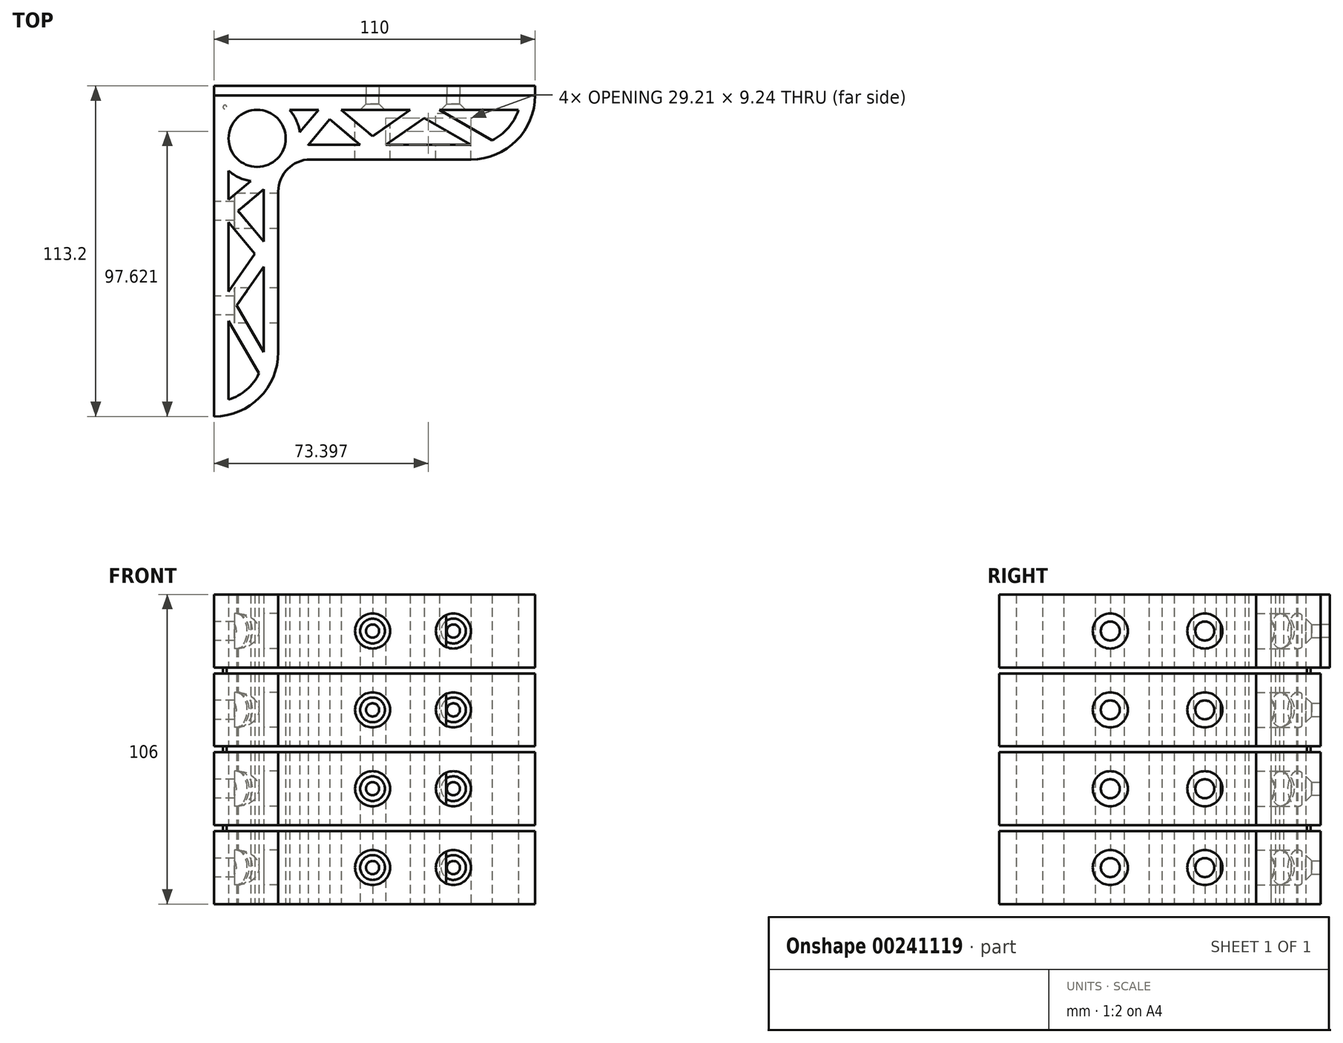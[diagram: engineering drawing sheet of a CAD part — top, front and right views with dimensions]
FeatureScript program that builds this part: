
annotation { "Feature Type Name" : "Feature", "Feature Type Description" : "" }
export const myFeature = defineFeature(function(context is Context, id is Id, definition is map)
    precondition{}
    {
        {
            var Q0;
            Q0=qCreatedBy(makeId("Top.planeOp"),FACE);
            var sketch = newSketch(context, id + "F0", { "sketchPlane" : qUnion([Q0])});
            skLineSegment(sketch, "E0", {"start": v(0, 0) * mm, "end": v(0, 110) * mm});
            skLineSegment(sketch, "E1", {"start": v(0, 110) * mm, "end": v(110, 0) * mm, "construction": true});
            skLineSegment(sketch, "E2", {"start": v(110, 0) * mm, "end": v(0, 0) * mm, "construction": true});
            skArc(sketch, "E3", {"start": v(0, 0) * mm, "mid": v(15.56, 6.44) * mm, "end": v(22, 22) * mm});
            skLineSegment(sketch, "E4", {"start": v(22, 22) * mm, "end": v(22, 77) * mm});
            skArc(sketch, "E5", {"start": v(25.22, 84.78) * mm, "mid": v(22.84, 81.2) * mm, "end": v(22, 77) * mm});
            skLineSegment(sketch, "E6", {"start": v(0, 110) * mm, "end": v(25.22, 84.78) * mm});
            skLineSegment(sketch, "E7.0", {"start": v(5, 5.75) * mm, "end": v(5, 105) * mm});
            skArc(sketch, "E7.1", {"start": v(5, 5.75) * mm, "mid": v(13.67, 11.9) * mm, "end": v(17, 22) * mm});
            skLineSegment(sketch, "E7.2", {"start": v(17, 22) * mm, "end": v(17, 77) * mm});
            skArc(sketch, "E7.3", {"start": v(21.69, 88.31) * mm, "mid": v(18.22, 83.12) * mm, "end": v(17, 77) * mm});
            skLineSegment(sketch, "E8", {"start": v(15.4, 14.78) * mm, "end": v(5, 32.78) * mm});
            skLineSegment(sketch, "E9", {"start": v(5, 42.78) * mm, "end": v(17, 22) * mm});
            skLineSegment(sketch, "E10", {"start": v(5, 42.78) * mm, "end": v(17, 59.92) * mm});
            skLineSegment(sketch, "E11", {"start": v(17, 59.92) * mm, "end": v(5, 74.22) * mm});
            skLineSegment(sketch, "E12", {"start": v(5, 66.44) * mm, "end": v(14.03, 55.68) * mm});
            skLineSegment(sketch, "E13", {"start": v(7.76, 38) * mm, "end": v(17, 51.2) * mm});
            skLineSegment(sketch, "E14", {"start": v(5, 32.78) * mm, "end": v(9.33, 35.28) * mm, "construction": true});
            skLineSegment(sketch, "E15", {"start": v(5, 42.78) * mm, "end": v(9.1, 39.92) * mm, "construction": true});
            skLineSegment(sketch, "E16", {"start": v(17, 59.92) * mm, "end": v(13.17, 56.7) * mm, "construction": true});
            skLineSegment(sketch, "E17", {"start": v(5, 74.22) * mm, "end": v(21.25, 87.85) * mm});
            skLineSegment(sketch, "E18", {"start": v(8.21, 70.4) * mm, "end": v(17, 77.77) * mm});
            skLineSegment(sketch, "E19", {"start": v(17, 77.77) * mm, "end": v(13.79, 81.6) * mm, "construction": true});
            skLineSegment(sketch, "E20", {"start": v(17, 77.77) * mm, "end": v(17.02, 77.78) * mm});
            skCircle(sketch, "E21", {"center": v(14.77, 95.23) * mm, "radius": 9.77 * mm});
            skArc(sketch, "E22", {"start": v(5, 84.15) * mm, "mid": v(8.55, 81.83) * mm, "end": v(12.61, 80.61) * mm});
            skLineSegment(sketch, "E23", {"start": v(14.77, 95.23) * mm, "end": v(5, 84.15) * mm, "construction": true});
            skPoint(sketch, "E24", {"position": v(8.3, 87.9) * mm});
            skSolve(sketch);
        }
        {
            var Q0;
            {var subQ0=sQuery(id+"F0.wireOp",EDGE,"E7.0");var subQ1=sQuery(id+"F0.wireOp",EDGE,"E6");var subQ2=makeQuery(id+"F0.imprint","INTERSECT",VERTEX,{"derivedFrom":[subQ1,subQ0]});Q0=makeQuery(id+"F0.imprint","IMPRINT",FACE,{"disambiguationData":[TD([[makeQuery(id+"F0.imprint","IMPRINT",EDGE,{"disambiguationData":[TD([[subQ2,-1.0]])],"derivedFrom":subQ1}),-1.0]])]});}
            var Q1;
            {var subQ14=sQuery(id+"F0.wireOp",EDGE,"E0");Q1=makeQuery(id+"F0.imprint","IMPRINT",FACE,{"disambiguationData":[TD([[makeQuery(id+"F0.imprint","IMPRINT",EDGE,{"derivedFrom":subQ14}),-1.0]])]});}
            var Q2;
            {var subQ3=sQuery(id+"F0.wireOp",EDGE,"E22");Q2=makeQuery(id+"F0.imprint","IMPRINT",FACE,{"disambiguationData":[TD([[makeQuery(id+"F0.imprint","IMPRINT",EDGE,{"derivedFrom":subQ3}),1.0]])]});}
            var Q3;
            {var subQ6=sQuery(id+"F0.wireOp",EDGE,"E18");Q3=makeQuery(id+"F0.imprint","IMPRINT",FACE,{"disambiguationData":[TD([[makeQuery(id+"F0.imprint","IMPRINT",EDGE,{"derivedFrom":subQ6}),1.0]])]});}
            var Q4;
            {var subQ6=sQuery(id+"F0.wireOp",EDGE,"E12");Q4=makeQuery(id+"F0.imprint","IMPRINT",FACE,{"disambiguationData":[TD([[makeQuery(id+"F0.imprint","IMPRINT",EDGE,{"derivedFrom":subQ6}),1.0]])]});}
            var Q5;
            {var subQ6=sQuery(id+"F0.wireOp",EDGE,"E13");Q5=makeQuery(id+"F0.imprint","IMPRINT",FACE,{"disambiguationData":[TD([[makeQuery(id+"F0.imprint","IMPRINT",EDGE,{"derivedFrom":subQ6}),1.0]])]});}
            var Q6;
            {var subQ0=sQuery(id+"F0.wireOp",EDGE,"E8");Q6=makeQuery(id+"F0.imprint","IMPRINT",FACE,{"disambiguationData":[TD([[makeQuery(id+"F0.imprint","IMPRINT",EDGE,{"derivedFrom":subQ0}),-1.0]])]});}
            extrude(context, id + "F1", {"entities" : qUnion([Q0, Q1, Q2, Q3, Q4, Q5, Q6]), "depth" : 25 * mm});
        }
        {
            var Q0;
            Q0=makeQuery(id+"F1.opExtrude","SWEPT_BODY",BODY,{"disambiguationData":[OSD([sQuery(id+"F0.wireOp",EDGE,"E0"),sQuery(id+"F0.wireOp",EDGE,"E3"),sQuery(id+"F0.wireOp",EDGE,"E4"),sQuery(id+"F0.wireOp",EDGE,"E5"),sQuery(id+"F0.wireOp",EDGE,"E6"),sQuery(id+"F0.wireOp",EDGE,"E7.0"),sQuery(id+"F0.wireOp",EDGE,"E7.1"),sQuery(id+"F0.wireOp",EDGE,"E7.2"),sQuery(id+"F0.wireOp",EDGE,"E7.3"),sQuery(id+"F0.wireOp",EDGE,"E8"),sQuery(id+"F0.wireOp",EDGE,"E9"),sQuery(id+"F0.wireOp",EDGE,"E10"),sQuery(id+"F0.wireOp",EDGE,"E11"),sQuery(id+"F0.wireOp",EDGE,"E12"),sQuery(id+"F0.wireOp",EDGE,"E13"),sQuery(id+"F0.wireOp",EDGE,"E17"),sQuery(id+"F0.wireOp",EDGE,"E18"),sQuery(id+"F0.wireOp",EDGE,"1766ab4e-5819-43f3-8559-5bc0afbba3c0.1"),sQuery(id+"F0.wireOp",EDGE,"1766ab4e-5819-43f3-8559-5bc0afbba3c0.2"),sQuery(id+"F0.wireOp",EDGE,"9d0f0dcf-438d-4fe8-bd9b-4e4da783941b.1"),sQuery(id+"F0.wireOp",EDGE,"9d0f0dcf-438d-4fe8-bd9b-4e4da783941b.3"),sQuery(id+"F0.wireOp",EDGE,"9d0f0dcf-438d-4fe8-bd9b-4e4da783941b.4"),sQuery(id+"F0.wireOp",EDGE,"E20")])]});
            var Q1;
            {var subQ0=sQuery(id+"F0.wireOp",EDGE,"E6");var subQ1=makeQuery(id+"F0.imprint","INTERSECT",VERTEX,{"derivedFrom":[subQ0,sQuery(id+"F0.wireOp",EDGE,"1766ab4e-5819-43f3-8559-5bc0afbba3c0.3")]});var subQ2=makeQuery(id+"F0.imprint","INTERSECT",VERTEX,{"derivedFrom":[subQ0,sQuery(id+"F0.wireOp",EDGE,"E7.0")]});Q1=makeQuery(id+"F1.opExtrude","SWEPT_FACE",FACE,{"disambiguationData":[OSD([subQ0]),TDD([makeQuery(id+"F0.imprint","IMPRINT",EDGE,{"disambiguationData":[TD([[makeQuery(id+"F0.imprint","INTERSECT",VERTEX,{"derivedFrom":[sQuery(id+"F0.wireOp",EDGE,"E0"),subQ0]}),-1.0]])],"derivedFrom":subQ0}),makeQuery(id+"F0.imprint","IMPRINT",EDGE,{"disambiguationData":[TD([[subQ2,-1.0]])],"derivedFrom":subQ0}),makeQuery(id+"F0.imprint","IMPRINT",EDGE,{"disambiguationData":[TD([[subQ1,-1.0]])],"derivedFrom":subQ0})])]});}
            mirror(context, id + "F2", {"operationType" : NewBodyOperationType.ADD, "entities" : qUnion([Q0]), "mirrorPlane" : qUnion([Q1])});
        }
        {
            var Q0;
            Q0=makeQuery(id+"F1.opExtrude","SWEPT_FACE",FACE,{"disambiguationData":[OSD([sQuery(id+"F0.wireOp",EDGE,"E0")])]});
            var sketch = newSketch(context, id + "F3", { "sketchPlane" : qUnion([Q0])});
            skLineSegment(sketch, "E25", {"start": v(-110, 12.5) * mm, "end": v(0, 12.5) * mm, "construction": true});
            skCircle(sketch, "E26", {"center": v(-70.4, 12.5) * mm, "radius": 3.25 * mm});
            skCircle(sketch, "E27", {"center": v(-38, 12.5) * mm, "radius": 3.25 * mm});
            skCircle(sketch, "E28", {"center": v(-70.4, 12.5) * mm, "radius": 6 * mm});
            skCircle(sketch, "E29", {"center": v(-38, 12.5) * mm, "radius": 6 * mm});
            skSolve(sketch);
        }
        {
            var Q0;
            Q0=makeQuery(id+"F2.opPattern","COPY",FACE,{"derivedFrom":makeQuery(id+"F1.opExtrude","SWEPT_FACE",FACE,{"disambiguationData":[OSD([sQuery(id+"F0.wireOp",EDGE,"E0")])]}),"instanceName":"1"});
            var sketch = newSketch(context, id + "F4", { "sketchPlane" : qUnion([Q0])});
            skLineSegment(sketch, "E30", {"start": v(0, 12.5) * mm, "end": v(-110, 12.5) * mm, "construction": true});
            skCircle(sketch, "E31", {"center": v(-54.32, 12.5) * mm, "radius": 2.25 * mm});
            skCircle(sketch, "E32", {"center": v(-82, 12.5) * mm, "radius": 2.25 * mm});
            skCircle(sketch, "E33", {"center": v(-82, 12.5) * mm, "radius": 6 * mm});
            skCircle(sketch, "E34", {"center": v(-54.32, 12.5) * mm, "radius": 6 * mm});
            skPoint(sketch, "E35", {"position": v(-88, 12.5) * mm});
            skSolve(sketch);
        }
        {
            var Q0;
            Q0=makeQuery(id+"F3.imprint","IMPRINT",FACE,{"disambiguationData":[TD([[makeQuery(id+"F3.imprint","IMPRINT",EDGE,{"derivedFrom":sQuery(id+"F3.wireOp",EDGE,"E26")}),1.0]])]});
            var Q1;
            Q1=makeQuery(id+"F3.imprint","IMPRINT",FACE,{"disambiguationData":[TD([[makeQuery(id+"F3.imprint","IMPRINT",EDGE,{"derivedFrom":sQuery(id+"F3.wireOp",EDGE,"E27")}),1.0]])]});
            extrude(context, id + "F5", {"entities" : qUnion([Q0, Q1]), "operationType" : NewBodyOperationType.REMOVE, "oppositeDirection" : true, "depth" : 25 * mm});
        }
        {
            var Q0;
            Q0=makeQuery(id+"F3.imprint","IMPRINT",FACE,{"disambiguationData":[TD([[makeQuery(id+"F3.imprint","IMPRINT",EDGE,{"derivedFrom":sQuery(id+"F3.wireOp",EDGE,"E26")}),-1.0]])]});
            var Q1;
            Q1=makeQuery(id+"F3.imprint","IMPRINT",FACE,{"disambiguationData":[TD([[makeQuery(id+"F3.imprint","IMPRINT",EDGE,{"derivedFrom":sQuery(id+"F3.wireOp",EDGE,"E27")}),-1.0]])]});
            extrude(context, id + "F6", {"entities" : qUnion([Q0, Q1]), "operationType" : NewBodyOperationType.REMOVE, "oppositeDirection" : true, "depth" : 25 * mm, "hasSecondDirection" : true, "secondDirectionOppositeDirection" : true, "secondDirectionDepth" : 7 * mm});
        }
        {
            var Q0;
            Q0=makeQuery(id+"F4.imprint","IMPRINT",FACE,{"disambiguationData":[TD([[makeQuery(id+"F4.imprint","IMPRINT",EDGE,{"derivedFrom":sQuery(id+"F4.wireOp",EDGE,"E32")}),1.0]])]});
            var Q1;
            Q1=makeQuery(id+"F4.imprint","IMPRINT",FACE,{"disambiguationData":[TD([[makeQuery(id+"F4.imprint","IMPRINT",EDGE,{"derivedFrom":sQuery(id+"F4.wireOp",EDGE,"E31")}),1.0]])]});
            extrude(context, id + "F7", {"entities" : qUnion([Q0, Q1]), "operationType" : NewBodyOperationType.REMOVE, "oppositeDirection" : true, "depth" : 25 * mm});
        }
        {
            var Q0;
            Q0=makeQuery(id+"F4.imprint","IMPRINT",FACE,{"disambiguationData":[TD([[makeQuery(id+"F4.imprint","IMPRINT",EDGE,{"derivedFrom":sQuery(id+"F4.wireOp",EDGE,"E31")}),-1.0]])]});
            var Q1;
            Q1=makeQuery(id+"F4.imprint","IMPRINT",FACE,{"disambiguationData":[TD([[makeQuery(id+"F4.imprint","IMPRINT",EDGE,{"derivedFrom":sQuery(id+"F4.wireOp",EDGE,"E32")}),-1.0]])]});
            extrude(context, id + "F8", {"entities" : qUnion([Q0, Q1]), "operationType" : NewBodyOperationType.REMOVE, "oppositeDirection" : true, "depth" : 25 * mm, "hasSecondDirection" : true, "secondDirectionOppositeDirection" : true, "secondDirectionDepth" : 6.3 * mm});
        }
        {
            var Q0;
            {var subQ0=sQuery(id+"F0.wireOp",EDGE,"E7.0");Q0=makeQuery(id+"F7.boolean.opBoolean","INTERSECT",EDGE,{"derivedFrom":[makeQuery(id+"F2.opPattern","COPY",FACE,{"derivedFrom":makeQuery(id+"F1.opExtrude","SWEPT_FACE",FACE,{"disambiguationData":[OSD([subQ0]),TDD([makeQuery(id+"F0.imprint","IMPRINT",EDGE,{"disambiguationData":[TD([[makeQuery(id+"F0.imprint","INTERSECT",VERTEX,{"derivedFrom":[subQ0,sQuery(id+"F0.wireOp",EDGE,"E12")]}),1.0]])],"derivedFrom":subQ0})])]}),"instanceName":"1"}),makeQuery(id+"F7.opExtrude","SWEPT_FACE",FACE,{"disambiguationData":[OSD([sQuery(id+"F4.wireOp",EDGE,"E31")])]})]});}
            var Q1;
            {var subQ0=sQuery(id+"F0.wireOp",EDGE,"E7.0");Q1=makeQuery(id+"F7.boolean.opBoolean","INTERSECT",EDGE,{"derivedFrom":[makeQuery(id+"F2.opPattern","COPY",FACE,{"derivedFrom":makeQuery(id+"F1.opExtrude","SWEPT_FACE",FACE,{"disambiguationData":[OSD([subQ0]),TDD([makeQuery(id+"F0.imprint","IMPRINT",EDGE,{"disambiguationData":[TD([[makeQuery(id+"F0.imprint","INTERSECT",VERTEX,{"derivedFrom":[subQ0,sQuery(id+"F0.wireOp",EDGE,"E7.1")]}),-1.0]])],"derivedFrom":subQ0})])]}),"instanceName":"1"}),makeQuery(id+"F7.opExtrude","SWEPT_FACE",FACE,{"disambiguationData":[OSD([sQuery(id+"F4.wireOp",EDGE,"E32")])]})]});}
            chamfer(context, id + "F9", {"entities" : qUnion([Q0, Q1]), "width" : 2 * mm, "tangentPropagation" : true});
        }
        {
            var Q0;
            Q0=makeQuery(id+"F1.opExtrude","SWEPT_BODY",BODY,{"disambiguationData":[OSD([sQuery(id+"F0.wireOp",EDGE,"E0"),sQuery(id+"F0.wireOp",EDGE,"E3"),sQuery(id+"F0.wireOp",EDGE,"E4"),sQuery(id+"F0.wireOp",EDGE,"E5"),sQuery(id+"F0.wireOp",EDGE,"E6"),sQuery(id+"F0.wireOp",EDGE,"E7.0"),sQuery(id+"F0.wireOp",EDGE,"E7.1"),sQuery(id+"F0.wireOp",EDGE,"E7.2"),sQuery(id+"F0.wireOp",EDGE,"E7.3"),sQuery(id+"F0.wireOp",EDGE,"E8"),sQuery(id+"F0.wireOp",EDGE,"E9"),sQuery(id+"F0.wireOp",EDGE,"E10"),sQuery(id+"F0.wireOp",EDGE,"E11"),sQuery(id+"F0.wireOp",EDGE,"E12"),sQuery(id+"F0.wireOp",EDGE,"E13"),sQuery(id+"F0.wireOp",EDGE,"E17"),sQuery(id+"F0.wireOp",EDGE,"E18"),sQuery(id+"F0.wireOp",EDGE,"E20"),sQuery(id+"F0.wireOp",EDGE,"E21"),sQuery(id+"F0.wireOp",EDGE,"E22")])]});
            transform(context, id + "F10", {"entities" : qUnion([Q0]), "transformType" : TransformType.TRANSLATION_3D, "dx" : 0 * mm, "dy" : 0 * mm, "dz" : 27 * mm, "makeCopy" : true});
        }
        {
            var Q0;
            Q0=makeQuery(id+"F10.opPattern","COPY",BODY,{"derivedFrom":makeQuery(id+"F1.opExtrude","SWEPT_BODY",BODY,{"disambiguationData":[OSD([sQuery(id+"F0.wireOp",EDGE,"E0"),sQuery(id+"F0.wireOp",EDGE,"E3"),sQuery(id+"F0.wireOp",EDGE,"E4"),sQuery(id+"F0.wireOp",EDGE,"E5"),sQuery(id+"F0.wireOp",EDGE,"E6"),sQuery(id+"F0.wireOp",EDGE,"E7.0"),sQuery(id+"F0.wireOp",EDGE,"E7.1"),sQuery(id+"F0.wireOp",EDGE,"E7.2"),sQuery(id+"F0.wireOp",EDGE,"E7.3"),sQuery(id+"F0.wireOp",EDGE,"E8"),sQuery(id+"F0.wireOp",EDGE,"E9"),sQuery(id+"F0.wireOp",EDGE,"E10"),sQuery(id+"F0.wireOp",EDGE,"E11"),sQuery(id+"F0.wireOp",EDGE,"E12"),sQuery(id+"F0.wireOp",EDGE,"E13"),sQuery(id+"F0.wireOp",EDGE,"E17"),sQuery(id+"F0.wireOp",EDGE,"E18"),sQuery(id+"F0.wireOp",EDGE,"E20"),sQuery(id+"F0.wireOp",EDGE,"E21"),sQuery(id+"F0.wireOp",EDGE,"E22")])]}),"instanceName":"1"});
            transform(context, id + "F11", {"entities" : qUnion([Q0]), "transformType" : TransformType.TRANSLATION_3D, "dx" : 0 * mm, "dy" : 0 * mm, "dz" : 27 * mm, "makeCopy" : true});
        }
        {
            var Q0;
            Q0=makeQuery(id+"F11.opPattern","COPY",BODY,{"derivedFrom":makeQuery(id+"F10.opPattern","COPY",BODY,{"derivedFrom":makeQuery(id+"F1.opExtrude","SWEPT_BODY",BODY,{"disambiguationData":[OSD([sQuery(id+"F0.wireOp",EDGE,"E0"),sQuery(id+"F0.wireOp",EDGE,"E3"),sQuery(id+"F0.wireOp",EDGE,"E4"),sQuery(id+"F0.wireOp",EDGE,"E5"),sQuery(id+"F0.wireOp",EDGE,"E6"),sQuery(id+"F0.wireOp",EDGE,"E7.0"),sQuery(id+"F0.wireOp",EDGE,"E7.1"),sQuery(id+"F0.wireOp",EDGE,"E7.2"),sQuery(id+"F0.wireOp",EDGE,"E7.3"),sQuery(id+"F0.wireOp",EDGE,"E8"),sQuery(id+"F0.wireOp",EDGE,"E9"),sQuery(id+"F0.wireOp",EDGE,"E10"),sQuery(id+"F0.wireOp",EDGE,"E11"),sQuery(id+"F0.wireOp",EDGE,"E12"),sQuery(id+"F0.wireOp",EDGE,"E13"),sQuery(id+"F0.wireOp",EDGE,"E17"),sQuery(id+"F0.wireOp",EDGE,"E18"),sQuery(id+"F0.wireOp",EDGE,"E20"),sQuery(id+"F0.wireOp",EDGE,"E21"),sQuery(id+"F0.wireOp",EDGE,"E22")])]}),"instanceName":"1"}),"instanceName":"1"});
            transform(context, id + "F12", {"entities" : qUnion([Q0]), "transformType" : TransformType.TRANSLATION_3D, "dx" : 0 * mm, "dy" : 0 * mm, "dz" : 27 * mm, "makeCopy" : true});
        }
        {
            var Q0;
            {var subQ0=makeQuery(id+"F1.opExtrude","CAP_FACE",FACE,{"disambiguationData":[OSD([sQuery(id+"F0.wireOp",EDGE,"E0"),sQuery(id+"F0.wireOp",EDGE,"E3"),sQuery(id+"F0.wireOp",EDGE,"E4"),sQuery(id+"F0.wireOp",EDGE,"E5"),sQuery(id+"F0.wireOp",EDGE,"E6"),sQuery(id+"F0.wireOp",EDGE,"E7.0"),sQuery(id+"F0.wireOp",EDGE,"E7.1"),sQuery(id+"F0.wireOp",EDGE,"E7.2"),sQuery(id+"F0.wireOp",EDGE,"E7.3"),sQuery(id+"F0.wireOp",EDGE,"E8"),sQuery(id+"F0.wireOp",EDGE,"E9"),sQuery(id+"F0.wireOp",EDGE,"E10"),sQuery(id+"F0.wireOp",EDGE,"E11"),sQuery(id+"F0.wireOp",EDGE,"E12"),sQuery(id+"F0.wireOp",EDGE,"E13"),sQuery(id+"F0.wireOp",EDGE,"E17"),sQuery(id+"F0.wireOp",EDGE,"E18"),sQuery(id+"F0.wireOp",EDGE,"E20"),sQuery(id+"F0.wireOp",EDGE,"E21"),sQuery(id+"F0.wireOp",EDGE,"E22")])],"isStart":false});Q0=makeQuery(id+"F12.opPattern","COPY",FACE,{"derivedFrom":makeQuery(id+"F11.opPattern","COPY",FACE,{"derivedFrom":makeQuery(id+"F10.opPattern","COPY",FACE,{"derivedFrom":makeQuery(id+"F2.boolean.opBoolean","MERGE",FACE,{"derivedFrom":[subQ0,makeQuery(id+"F2.opPattern","COPY",FACE,{"derivedFrom":subQ0,"instanceName":"1"})]}),"instanceName":"1"}),"instanceName":"1"}),"instanceName":"1"});}
            var sketch = newSketch(context, id + "F13", { "sketchPlane" : qUnion([Q0])});
            skCircle(sketch, "E36", {"center": v(3.73, 105.98) * mm, "radius": 0.64 * mm});
            skSolve(sketch);
        }
        {
            var Q0;
            Q0=makeQuery(id+"F13.imprint","IMPRINT",FACE,{"disambiguationData":[TD([[makeQuery(id+"F13.imprint","IMPRINT",EDGE,{"derivedFrom":sQuery(id+"F13.wireOp",EDGE,"E36")}),1.0]])]});
            var Q1;
            {var subQ0=makeQuery(id+"F1.opExtrude","CAP_FACE",FACE,{"disambiguationData":[OSD([sQuery(id+"F0.wireOp",EDGE,"E0"),sQuery(id+"F0.wireOp",EDGE,"E3"),sQuery(id+"F0.wireOp",EDGE,"E4"),sQuery(id+"F0.wireOp",EDGE,"E5"),sQuery(id+"F0.wireOp",EDGE,"E6"),sQuery(id+"F0.wireOp",EDGE,"E7.0"),sQuery(id+"F0.wireOp",EDGE,"E7.1"),sQuery(id+"F0.wireOp",EDGE,"E7.2"),sQuery(id+"F0.wireOp",EDGE,"E7.3"),sQuery(id+"F0.wireOp",EDGE,"E8"),sQuery(id+"F0.wireOp",EDGE,"E9"),sQuery(id+"F0.wireOp",EDGE,"E10"),sQuery(id+"F0.wireOp",EDGE,"E11"),sQuery(id+"F0.wireOp",EDGE,"E12"),sQuery(id+"F0.wireOp",EDGE,"E13"),sQuery(id+"F0.wireOp",EDGE,"E17"),sQuery(id+"F0.wireOp",EDGE,"E18"),sQuery(id+"F0.wireOp",EDGE,"E20"),sQuery(id+"F0.wireOp",EDGE,"E21"),sQuery(id+"F0.wireOp",EDGE,"E22")])],"isStart":true});Q1=makeQuery(id+"F2.boolean.opBoolean","MERGE",FACE,{"derivedFrom":[subQ0,makeQuery(id+"F2.opPattern","COPY",FACE,{"derivedFrom":subQ0,"instanceName":"1"})]});}
            extrude(context, id + "F14", {"entities" : qUnion([Q0]), "operationType" : NewBodyOperationType.ADD, "endBound" : BoundingType.UP_TO_SURFACE, "oppositeDirection" : true, "endBoundEntityFace" : qUnion([Q1]), "depth" : 25 * mm});
        }
        {
            var Q0;
            Q0=makeQuery(id+"F12.opPattern","COPY",FACE,{"derivedFrom":makeQuery(id+"F11.opPattern","COPY",FACE,{"derivedFrom":makeQuery(id+"F10.opPattern","COPY",FACE,{"derivedFrom":makeQuery(id+"F2.opPattern","COPY",FACE,{"derivedFrom":makeQuery(id+"F1.opExtrude","SWEPT_FACE",FACE,{"disambiguationData":[OSD([sQuery(id+"F0.wireOp",EDGE,"E0")])]}),"instanceName":"1"}),"instanceName":"1"}),"instanceName":"1"}),"instanceName":"1"});
            extrude(context, id + "F15", {"entities" : qUnion([Q0]), "depth" : 3.2 * mm});
        }
    });
